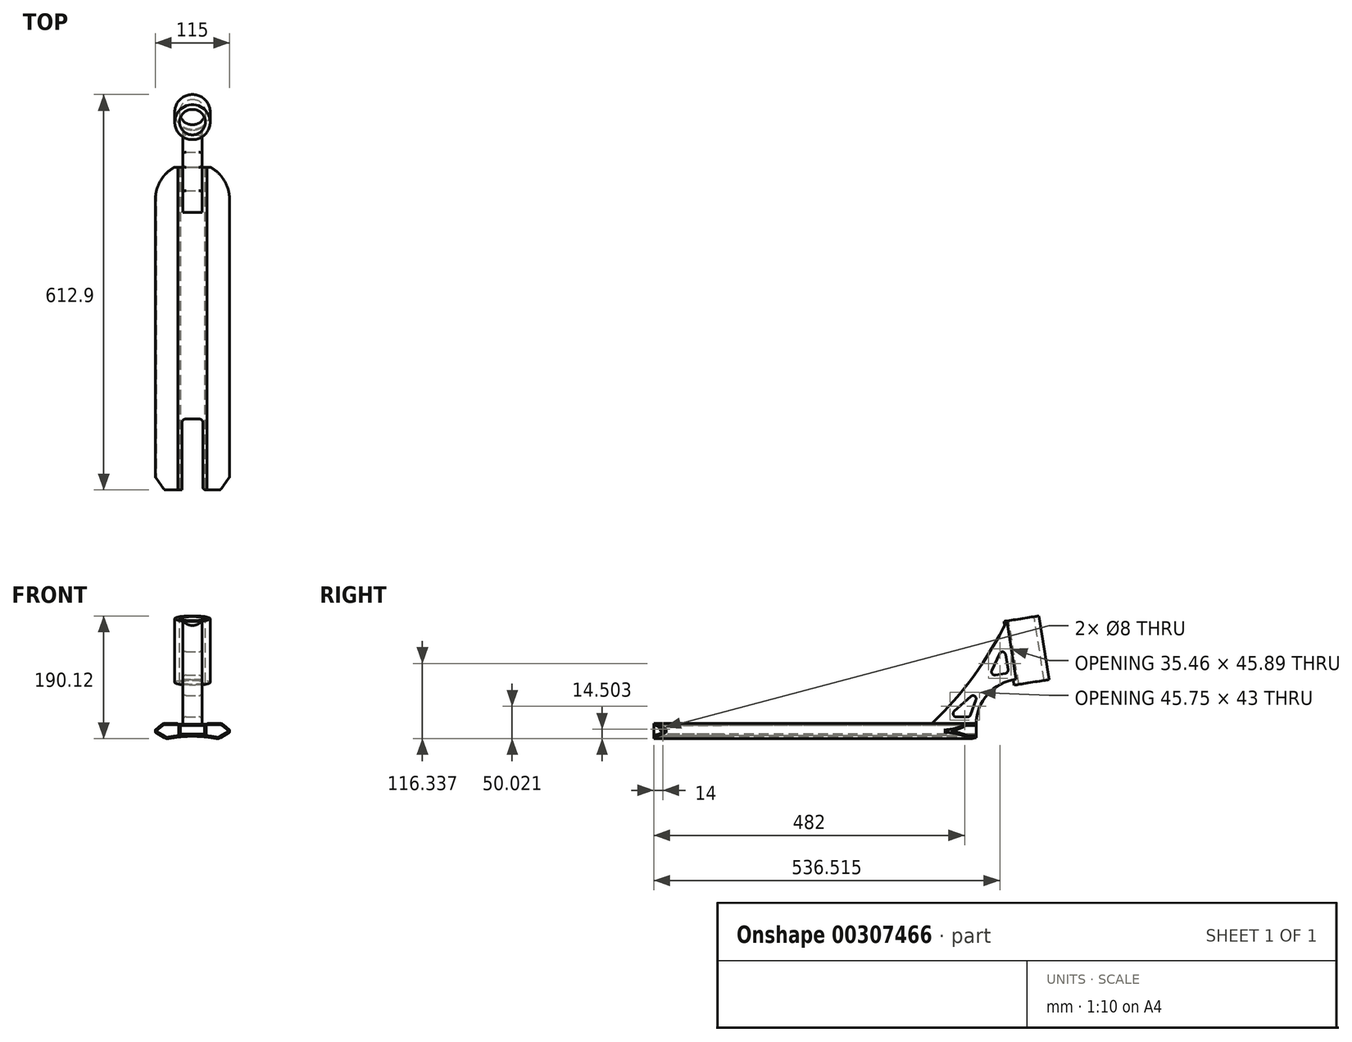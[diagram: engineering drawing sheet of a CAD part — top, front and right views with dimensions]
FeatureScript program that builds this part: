
annotation { "Feature Type Name" : "Feature", "Feature Type Description" : "" }
export const myFeature = defineFeature(function(context is Context, id is Id, definition is map)
    precondition{}
    {
        {
            var Q0;
            Q0=qCreatedBy(makeId("Front.planeOp"),FACE);
            var sketch = newSketch(context, id + "F0", { "sketchPlane" : qUnion([Q0])});
            skLineSegment(sketch, "E0", {"start": v(0, 0) * mm, "end": v(0, 75.33) * mm, "construction": true});
            skLineSegment(sketch, "E1", {"start": v(0, 22.7) * mm, "end": v(22.5, 22.7) * mm});
            skLineSegment(sketch, "E2", {"start": v(22.5, 24) * mm, "end": v(22.5, 22.7) * mm});
            skLineSegment(sketch, "E3", {"start": v(45.58, 24) * mm, "end": v(22.5, 24) * mm});
            skLineSegment(sketch, "E4", {"start": v(57.5, 14) * mm, "end": v(45.58, 24) * mm});
            skLineSegment(sketch, "E5", {"start": v(57.5, 14) * mm, "end": v(57.5, 10) * mm});
            skLineSegment(sketch, "E6", {"start": v(57.5, 10) * mm, "end": v(40.18, 0) * mm});
            skLineSegment(sketch, "E7.MirrorCS", {"start": v(0, 22.7) * mm, "end": v(-22.5, 22.7) * mm});
            skLineSegment(sketch, "E8.MirrorCS", {"start": v(-45.58, 24) * mm, "end": v(-22.5, 24) * mm});
            skLineSegment(sketch, "E9.MirrorCS", {"start": v(-22.5, 24) * mm, "end": v(-22.5, 22.7) * mm});
            skLineSegment(sketch, "E10.MirrorCS", {"start": v(-57.5, 14) * mm, "end": v(-45.58, 24) * mm});
            skLineSegment(sketch, "E11.MirrorCS", {"start": v(-57.5, 14) * mm, "end": v(-57.5, 10) * mm});
            skLineSegment(sketch, "E12.MirrorCS", {"start": v(-57.5, 10) * mm, "end": v(-40.18, 0) * mm});
            skArc(sketch, "E13", {"start": v(40.18, 0) * mm, "mid": v(0, 4.08) * mm, "end": v(-40.18, 0) * mm});
            skSolve(sketch);
        }
        {
            var Q0;
            Q0 = qSketchRegion(id + "F0", true);
            extrude(context, id + "F1", {"entities" : qUnion([Q0]), "endBound" : BoundingType.SYMMETRIC, "depth" : 500 * mm});
        }
        {
            var Q0;
            Q0=qCreatedBy(makeId("Front.planeOp"),FACE);
            var sketch = newSketch(context, id + "F2", { "sketchPlane" : qUnion([Q0])});
            skLineSegment(sketch, "E14.bottom", {"start": v(-19, 20.7) * mm, "end": v(19, 20.7) * mm});
            skLineSegment(sketch, "E14.top", {"start": v(-19, 7.7) * mm, "end": v(19, 7.7) * mm});
            skLineSegment(sketch, "E14.left", {"start": v(-19, 20.7) * mm, "end": v(-19, 7.7) * mm});
            skLineSegment(sketch, "E14.right", {"start": v(19, 20.7) * mm, "end": v(19, 7.7) * mm});
            skSolve(sketch);
        }
        {
            var Q0;
            Q0 = qSketchRegion(id + "F2", true);
            extrude(context, id + "F3", {"entities" : qUnion([Q0]), "operationType" : NewBodyOperationType.REMOVE, "endBound" : BoundingType.SYMMETRIC, "oppositeDirection" : true, "depth" : 500 * mm});
        }
        {
            var Q0;
            Q0=makeQuery(id+"F1.opExtrude","SWEPT_EDGE",EDGE,{"disambiguationData":[OSD([sQuery(id+"F0.wireOp",EDGE,"E6"),sQuery(id+"F0.wireOp",EDGE,"E13")])]});
            var Q1;
            Q1=makeQuery(id+"F1.opExtrude","SWEPT_EDGE",EDGE,{"disambiguationData":[OSD([sQuery(id+"F0.wireOp",EDGE,"E12.MirrorCS"),sQuery(id+"F0.wireOp",EDGE,"E13")])]});
            var Q2;
            Q2=makeQuery(id+"F1.opExtrude","SWEPT_EDGE",EDGE,{"disambiguationData":[OSD([sQuery(id+"F0.wireOp",EDGE,"E8.MirrorCS"),sQuery(id+"F0.wireOp",EDGE,"E10.MirrorCS")])]});
            var Q3;
            Q3=makeQuery(id+"F1.opExtrude","SWEPT_EDGE",EDGE,{"disambiguationData":[OSD([sQuery(id+"F0.wireOp",EDGE,"E3"),sQuery(id+"F0.wireOp",EDGE,"E4")])]});
            fillet(context, id + "F4", {"entities" : qUnion([Q0, Q1, Q2, Q3]), "radius" : 9 * mm, "tangentPropagation" : true, "allowEdgeOverflow" : false});
        }
        {
            var Q0;
            Q0=makeQuery(id+"F1.opExtrude","SWEPT_EDGE",EDGE,{"disambiguationData":[OSD([sQuery(id+"F0.wireOp",EDGE,"E4"),sQuery(id+"F0.wireOp",EDGE,"E5")])]});
            var Q1;
            Q1=makeQuery(id+"F1.opExtrude","SWEPT_EDGE",EDGE,{"disambiguationData":[OSD([sQuery(id+"F0.wireOp",EDGE,"E5"),sQuery(id+"F0.wireOp",EDGE,"E6")])]});
            var Q2;
            Q2=makeQuery(id+"F1.opExtrude","SWEPT_EDGE",EDGE,{"disambiguationData":[OSD([sQuery(id+"F0.wireOp",EDGE,"E10.MirrorCS"),sQuery(id+"F0.wireOp",EDGE,"E11.MirrorCS")])]});
            var Q3;
            Q3=makeQuery(id+"F1.opExtrude","SWEPT_EDGE",EDGE,{"disambiguationData":[OSD([sQuery(id+"F0.wireOp",EDGE,"E11.MirrorCS"),sQuery(id+"F0.wireOp",EDGE,"E12.MirrorCS")])]});
            fillet(context, id + "F5", {"entities" : qUnion([Q0, Q1, Q2, Q3]), "radius" : 1 * mm, "tangentPropagation" : true, "allowEdgeOverflow" : false});
        }
        {
            var Q0;
            Q0=makeQuery(id+"F1.opExtrude","SWEPT_EDGE",EDGE,{"disambiguationData":[OSD([sQuery(id+"F0.wireOp",EDGE,"E8.MirrorCS"),sQuery(id+"F0.wireOp",EDGE,"E9.MirrorCS")])]});
            var Q1;
            Q1=makeQuery(id+"F1.opExtrude","SWEPT_EDGE",EDGE,{"disambiguationData":[OSD([sQuery(id+"F0.wireOp",EDGE,"E2"),sQuery(id+"F0.wireOp",EDGE,"E3")])]});
            fillet(context, id + "F6", {"entities" : qUnion([Q0, Q1]), "radius" : 2 * mm, "tangentPropagation" : true, "allowEdgeOverflow" : false});
        }
        {
            var Q0;
            Q0=makeQuery(id+"F1.opExtrude","CAP_FACE",FACE,{"disambiguationData":[OSD([sQuery(id+"F0.wireOp",EDGE,"E1"),sQuery(id+"F0.wireOp",EDGE,"E2"),sQuery(id+"F0.wireOp",EDGE,"E3"),sQuery(id+"F0.wireOp",EDGE,"E4"),sQuery(id+"F0.wireOp",EDGE,"E5"),sQuery(id+"F0.wireOp",EDGE,"E6"),sQuery(id+"F0.wireOp",EDGE,"E7.MirrorCS"),sQuery(id+"F0.wireOp",EDGE,"E8.MirrorCS"),sQuery(id+"F0.wireOp",EDGE,"E9.MirrorCS"),sQuery(id+"F0.wireOp",EDGE,"E10.MirrorCS"),sQuery(id+"F0.wireOp",EDGE,"E11.MirrorCS"),sQuery(id+"F0.wireOp",EDGE,"E12.MirrorCS"),sQuery(id+"F0.wireOp",EDGE,"E13")])],"isStart":false});
            var sketch = newSketch(context, id + "F7", { "sketchPlane" : qUnion([Q0])});
            skLineSegment(sketch, "E15.0", {"start": v(-42.3, 22) * mm, "end": v(-24.37, 22) * mm});
            skArc(sketch, "E15.1", {"start": v(-42.3, 22) * mm, "mid": v(-44.7, 21.58) * mm, "end": v(-46.8, 20.36) * mm});
            skArc(sketch, "E15.2", {"start": v(37.3, 2.6) * mm, "mid": v(0, 6.08) * mm, "end": v(-37.3, 2.6) * mm});
            skArc(sketch, "E15.3", {"start": v(-42.1, 3.42) * mm, "mid": v(-39.78, 2.58) * mm, "end": v(-37.3, 2.6) * mm});
            skLineSegment(sketch, "E15.4", {"start": v(-55.61, 11.22) * mm, "end": v(-42.1, 3.42) * mm});
            skLineSegment(sketch, "E15.5", {"start": v(-55.76, 12.85) * mm, "end": v(-46.8, 20.36) * mm});
            skPoint(sketch, "E16.visualSharp", {"position": v(-56.85, 11.93) * mm});
            skArc(sketch, "E16.filletArc", {"start": v(-55.76, 12.85) * mm, "mid": v(-56.1, 12) * mm, "end": v(-55.61, 11.22) * mm});
            skArc(sketch, "E17", {"start": v(-22.5, 20.7) * mm, "mid": v(-23.23, 21.64) * mm, "end": v(-24.37, 22) * mm});
            skLineSegment(sketch, "E18", {"start": v(-22.5, 20.7) * mm, "end": v(-21, 20.7) * mm});
            skLineSegment(sketch, "E19", {"start": v(-21, 20.7) * mm, "end": v(-21, 4.98) * mm});
            skLineSegment(sketch, "E20.MirrorCS", {"start": v(21, 20.7) * mm, "end": v(21, 4.98) * mm});
            skLineSegment(sketch, "E21.MirrorCS", {"start": v(22.5, 20.7) * mm, "end": v(21, 20.7) * mm});
            skArc(sketch, "E22.MirrorCS", {"start": v(22.5, 20.7) * mm, "mid": v(23.23, 21.64) * mm, "end": v(24.37, 22) * mm});
            skLineSegment(sketch, "E23.MirrorCS", {"start": v(42.3, 22) * mm, "end": v(24.37, 22) * mm});
            skArc(sketch, "E24.MirrorCS", {"start": v(42.3, 22) * mm, "mid": v(44.7, 21.58) * mm, "end": v(46.8, 20.36) * mm});
            skLineSegment(sketch, "E25.MirrorCS", {"start": v(55.76, 12.85) * mm, "end": v(46.8, 20.36) * mm});
            skArc(sketch, "E26.MirrorCS", {"start": v(55.76, 12.85) * mm, "mid": v(56.1, 12) * mm, "end": v(55.61, 11.22) * mm});
            skLineSegment(sketch, "E27.MirrorCS", {"start": v(55.61, 11.22) * mm, "end": v(42.1, 3.42) * mm});
            skArc(sketch, "E28.MirrorCS", {"start": v(42.1, 3.42) * mm, "mid": v(39.78, 2.58) * mm, "end": v(37.3, 2.6) * mm});
            skArc(sketch, "E29.MirrorCS", {"start": v(-37.3, 2.6) * mm, "mid": v(0, 6.08) * mm, "end": v(37.3, 2.6) * mm});
            skSolve(sketch);
        }
        {
            var Q0;
            Q0=makeQuery(id+"F7.imprint","IMPRINT",FACE,{"disambiguationData":[TD([[makeQuery(id+"F7.imprint","IMPRINT",EDGE,{"derivedFrom":sQuery(id+"F7.wireOp",EDGE,"E15.0")}),-1.0]])]});
            var Q1;
            {var subQ0=sQuery(id+"F7.wireOp",EDGE,"E20.MirrorCS");Q1=makeQuery(id+"F7.imprint","IMPRINT",FACE,{"disambiguationData":[TD([[makeQuery(id+"F7.imprint","IMPRINT",EDGE,{"derivedFrom":subQ0}),1.0]])]});}
            extrude(context, id + "F8", {"entities" : qUnion([Q0, Q1]), "operationType" : NewBodyOperationType.REMOVE, "endBound" : BoundingType.THROUGH_ALL, "oppositeDirection" : true, "depth" : 25 * mm});
        }
        {
            var Q0;
            Q0=qCreatedBy(makeId("Top.planeOp"),FACE);
            var sketch = newSketch(context, id + "F9", { "sketchPlane" : qUnion([Q0])});
            skArc(sketch, "E30", {"start": v(57.5, 200) * mm, "mid": v(0, 257.5) * mm, "end": v(-57.5, 200) * mm});
            skLineSegment(sketch, "E31", {"start": v(-57.5, 200) * mm, "end": v(-57.5, 280) * mm});
            skLineSegment(sketch, "E32", {"start": v(57.5, 200) * mm, "end": v(57.5, 280) * mm});
            skLineSegment(sketch, "E33", {"start": v(-57.5, 280) * mm, "end": v(57.5, 280) * mm});
            skSolve(sketch);
        }
        {
            var Q0;
            Q0 = qSketchRegion(id + "F9", true);
            extrude(context, id + "F10", {"entities" : qUnion([Q0]), "operationType" : NewBodyOperationType.REMOVE, "endBound" : BoundingType.THROUGH_ALL, "oppositeDirection" : true, "depth" : 25 * mm, "hasSecondDirection" : true, "secondDirectionBound" : SecondDirectionBoundingType.THROUGH_ALL, "secondDirectionOppositeDirection" : false, "secondDirectionDepth" : 25 * mm});
        }
        {
            var Q0;
            Q0=qCreatedBy(makeId("Top.planeOp"),FACE);
            var sketch = newSketch(context, id + "F11", { "sketchPlane" : qUnion([Q0])});
            skLineSegment(sketch, "E34", {"start": v(-68, -216) * mm, "end": v(-68, -346) * mm});
            skLineSegment(sketch, "E35", {"start": v(-68, -346) * mm, "end": v(68, -346) * mm});
            skLineSegment(sketch, "E36", {"start": v(68, -346) * mm, "end": v(68, -216) * mm});
            skLineSegment(sketch, "E37", {"start": v(68, -216) * mm, "end": v(43.3, -250) * mm});
            skLineSegment(sketch, "E38", {"start": v(43.3, -250) * mm, "end": v(16, -250) * mm});
            skLineSegment(sketch, "E39", {"start": v(16, -250) * mm, "end": v(16, -140) * mm});
            skLineSegment(sketch, "E40", {"start": v(16, -140) * mm, "end": v(-16, -140) * mm});
            skLineSegment(sketch, "E41", {"start": v(-16, -140) * mm, "end": v(-16, -250) * mm});
            skLineSegment(sketch, "E42", {"start": v(-16, -250) * mm, "end": v(-43.3, -250) * mm});
            skLineSegment(sketch, "E43", {"start": v(-43.3, -250) * mm, "end": v(-68, -216) * mm});
            skSolve(sketch);
        }
        {
            var Q0;
            Q0 = qSketchRegion(id + "F11", true);
            extrude(context, id + "F12", {"entities" : qUnion([Q0]), "operationType" : NewBodyOperationType.REMOVE, "endBound" : BoundingType.THROUGH_ALL, "oppositeDirection" : true, "depth" : 25 * mm, "hasSecondDirection" : true, "secondDirectionBound" : SecondDirectionBoundingType.THROUGH_ALL, "secondDirectionOppositeDirection" : false, "secondDirectionDepth" : 25 * mm});
        }
        {
            var Q0;
            {var subQ0=sQuery(id+"F11.wireOp",EDGE,"E40");var subQ1=sQuery(id+"F11.wireOp",EDGE,"E41");Q0=makeQuery(id+"F12.boolean.opBoolean","COPY",EDGE,{"disambiguationData":[TD([makeQuery(id+"F3.boolean.opBoolean","COPY",FACE,{"derivedFrom":makeQuery(id+"F3.opExtrude","SWEPT_FACE",FACE,{"disambiguationData":[OSD([sQuery(id+"F2.wireOp",EDGE,"E14.bottom")])]})})])],"derivedFrom":makeQuery(id+"F12.opExtrude","SWEPT_EDGE",EDGE,{"disambiguationData":[OSD([subQ0,subQ1])]})});}
            var Q1;
            {var subQ0=sQuery(id+"F11.wireOp",EDGE,"E41");var subQ1=sQuery(id+"F11.wireOp",EDGE,"E40");Q1=makeQuery(id+"F12.boolean.opBoolean","COPY",EDGE,{"disambiguationData":[TD([makeQuery(id+"F1.opExtrude","SWEPT_FACE",FACE,{"disambiguationData":[OSD([sQuery(id+"F0.wireOp",EDGE,"E13")])]})])],"derivedFrom":makeQuery(id+"F12.opExtrude","SWEPT_EDGE",EDGE,{"disambiguationData":[OSD([subQ1,subQ0])]})});}
            var Q2;
            {var subQ0=sQuery(id+"F11.wireOp",EDGE,"E40");var subQ1=sQuery(id+"F11.wireOp",EDGE,"E39");Q2=makeQuery(id+"F12.boolean.opBoolean","COPY",EDGE,{"disambiguationData":[TD([makeQuery(id+"F3.boolean.opBoolean","COPY",FACE,{"derivedFrom":makeQuery(id+"F3.opExtrude","SWEPT_FACE",FACE,{"disambiguationData":[OSD([sQuery(id+"F2.wireOp",EDGE,"E14.bottom")])]})})])],"derivedFrom":makeQuery(id+"F12.opExtrude","SWEPT_EDGE",EDGE,{"disambiguationData":[OSD([subQ1,subQ0])]})});}
            var Q3;
            {var subQ0=sQuery(id+"F11.wireOp",EDGE,"E39");var subQ1=sQuery(id+"F11.wireOp",EDGE,"E40");Q3=makeQuery(id+"F12.boolean.opBoolean","COPY",EDGE,{"disambiguationData":[TD([makeQuery(id+"F1.opExtrude","SWEPT_FACE",FACE,{"disambiguationData":[OSD([sQuery(id+"F0.wireOp",EDGE,"E13")])]})])],"derivedFrom":makeQuery(id+"F12.opExtrude","SWEPT_EDGE",EDGE,{"disambiguationData":[OSD([subQ0,subQ1])]})});}
            var Q4;
            {var subQ2=sQuery(id+"F11.wireOp",EDGE,"E41");Q4=makeQuery(id+"F12.boolean.opBoolean","COPY",EDGE,{"disambiguationData":[TD([makeQuery(id+"F3.boolean.opBoolean","COPY",FACE,{"derivedFrom":makeQuery(id+"F3.opExtrude","SWEPT_FACE",FACE,{"disambiguationData":[OSD([sQuery(id+"F2.wireOp",EDGE,"E14.bottom")])]})})])],"derivedFrom":makeQuery(id+"F12.opExtrude","SWEPT_EDGE",EDGE,{"disambiguationData":[OSD([subQ2,sQuery(id+"F11.wireOp",EDGE,"E42")])]})});}
            var Q5;
            {var subQ0=sQuery(id+"F0.wireOp",EDGE,"E13");var subQ1=sQuery(id+"F11.wireOp",EDGE,"E41");Q5=makeQuery(id+"F12.boolean.opBoolean","COPY",EDGE,{"disambiguationData":[TD([makeQuery(id+"F1.opExtrude","SWEPT_FACE",FACE,{"disambiguationData":[OSD([subQ0])]})])],"derivedFrom":makeQuery(id+"F12.opExtrude","SWEPT_EDGE",EDGE,{"disambiguationData":[OSD([subQ1,sQuery(id+"F11.wireOp",EDGE,"E42")])]})});}
            var Q6;
            {var subQ0=sQuery(id+"F0.wireOp",EDGE,"E13");var subQ1=sQuery(id+"F11.wireOp",EDGE,"E39");Q6=makeQuery(id+"F12.boolean.opBoolean","COPY",EDGE,{"disambiguationData":[TD([makeQuery(id+"F1.opExtrude","SWEPT_FACE",FACE,{"disambiguationData":[OSD([subQ0])]})])],"derivedFrom":makeQuery(id+"F12.opExtrude","SWEPT_EDGE",EDGE,{"disambiguationData":[OSD([sQuery(id+"F11.wireOp",EDGE,"E38"),subQ1])]})});}
            var Q7;
            {var subQ2=sQuery(id+"F11.wireOp",EDGE,"E39");Q7=makeQuery(id+"F12.boolean.opBoolean","COPY",EDGE,{"disambiguationData":[TD([makeQuery(id+"F3.boolean.opBoolean","COPY",FACE,{"derivedFrom":makeQuery(id+"F3.opExtrude","SWEPT_FACE",FACE,{"disambiguationData":[OSD([sQuery(id+"F2.wireOp",EDGE,"E14.bottom")])]})})])],"derivedFrom":makeQuery(id+"F12.opExtrude","SWEPT_EDGE",EDGE,{"disambiguationData":[OSD([sQuery(id+"F11.wireOp",EDGE,"E38"),subQ2])]})});}
            fillet(context, id + "F13", {"entities" : qUnion([Q0, Q1, Q2, Q3, Q4, Q5, Q6, Q7]), "radius" : 5 * mm, "tangentPropagation" : true, "allowEdgeOverflow" : false});
        }
        {
            var Q0;
            Q0=qCreatedBy(makeId("Right.planeOp"),FACE);
            var sketch = newSketch(context, id + "F14", { "sketchPlane" : qUnion([Q0])});
            skLineSegment(sketch, "E44", {"start": v(180, 22.7) * mm, "end": v(250, 22.7) * mm});
            skArc(sketch, "E45", {"start": v(311.71, 92.2) * mm, "mid": v(267.66, 69.18) * mm, "end": v(250, 22.7) * mm});
            skArc(sketch, "E46", {"start": v(180, 22.7) * mm, "mid": v(245.97, 97.36) * mm, "end": v(297.38, 182.7) * mm});
            skLineSegment(sketch, "E47", {"start": v(297.38, 182.7) * mm, "end": v(342.82, 189.9) * mm});
            skLineSegment(sketch, "E48", {"start": v(342.82, 189.9) * mm, "end": v(358.46, 91.13) * mm});
            skLineSegment(sketch, "E49", {"start": v(358.46, 91.13) * mm, "end": v(313.03, 83.93) * mm});
            skLineSegment(sketch, "E50", {"start": v(313.03, 83.93) * mm, "end": v(311.71, 92.2) * mm});
            skSolve(sketch);
        }
        {
            var Q0;
            Q0=makeQuery(id+"F14.imprint","IMPRINT",FACE,{"disambiguationData":[TD([[makeQuery(id+"F14.imprint","IMPRINT",EDGE,{"derivedFrom":sQuery(id+"F14.wireOp",EDGE,"E44")}),1.0]])]});
            extrude(context, id + "F15", {"entities" : qUnion([Q0]), "operationType" : NewBodyOperationType.ADD, "endBound" : BoundingType.SYMMETRIC, "depth" : 30 * mm});
        }
        {
            var Q0;
            Q0=makeQuery(id+"F15.opExtrude","SWEPT_FACE",FACE,{"disambiguationData":[OSD([sQuery(id+"F14.wireOp",EDGE,"E47")])]});
            var sketch = newSketch(context, id + "F16", { "sketchPlane" : qUnion([Q0])});
            skCircle(sketch, "E51", {"center": v(0, 345.3) * mm, "radius": 27.5 * mm});
            skSolve(sketch);
        }
        {
            var Q0;
            Q0 = qSketchRegion(id + "F16", true);
            var Q1;
            Q1=makeQuery(id+"F15.opExtrude","SWEPT_FACE",FACE,{"disambiguationData":[OSD([sQuery(id+"F14.wireOp",EDGE,"E49")])]});
            extrude(context, id + "F17", {"entities" : qUnion([Q0]), "operationType" : NewBodyOperationType.ADD, "endBound" : BoundingType.UP_TO_SURFACE, "oppositeDirection" : true, "endBoundEntityFace" : qUnion([Q1]), "depth" : 25 * mm});
        }
        {
            var Q0;
            Q0=makeQuery(id+"F17.boolean.opBoolean","MERGE",FACE,{"derivedFrom":[makeQuery(id+"F15.opExtrude","SWEPT_FACE",FACE,{"disambiguationData":[OSD([sQuery(id+"F14.wireOp",EDGE,"E47")])]}),makeQuery(id+"F17.opExtrude","CAP_FACE",FACE,{"disambiguationData":[OSD([sQuery(id+"F16.wireOp",EDGE,"E51")])],"isStart":true})]});
            var sketch = newSketch(context, id + "F18", { "sketchPlane" : qUnion([Q0])});
            skPoint(sketch, "E52", {"position": v(0, 345.3) * mm});
            skSolve(sketch);
        }
        {
            var Q0;
            Q0=sQuery(id+"F18.wireOp",VERTEX,"E52");
            var Q1;
            Q1=makeQuery(id+"F1.opExtrude","SWEPT_BODY",BODY,{"disambiguationData":[OSD([sQuery(id+"F0.wireOp",EDGE,"E1"),sQuery(id+"F0.wireOp",EDGE,"E2"),sQuery(id+"F0.wireOp",EDGE,"E3"),sQuery(id+"F0.wireOp",EDGE,"E4"),sQuery(id+"F0.wireOp",EDGE,"E5"),sQuery(id+"F0.wireOp",EDGE,"E6"),sQuery(id+"F0.wireOp",EDGE,"E7.MirrorCS"),sQuery(id+"F0.wireOp",EDGE,"E8.MirrorCS"),sQuery(id+"F0.wireOp",EDGE,"E9.MirrorCS"),sQuery(id+"F0.wireOp",EDGE,"E10.MirrorCS"),sQuery(id+"F0.wireOp",EDGE,"E11.MirrorCS"),sQuery(id+"F0.wireOp",EDGE,"E12.MirrorCS"),sQuery(id+"F0.wireOp",EDGE,"E13")])]});
            hole(context, id + "F19", {"style" : HoleStyle.SIMPLE, "endStyle" : HoleEndStyle.THROUGH, "holeDiameter" : 40 * mm, "isTappedThrough" : true, "tappedDepth" : 12 * mm, "tapClearance" : 3, "locations" : qUnion([Q0]), "scope" : qUnion([Q1])});
        }
        {
            var Q0;
            Q0=makeQuery(id+"F8.boolean.opBoolean","COPY",FACE,{"derivedFrom":makeQuery(id+"F8.opExtrude","SWEPT_FACE",FACE,{"disambiguationData":[OSD([sQuery(id+"F7.wireOp",EDGE,"E20.MirrorCS")])]})});
            var sketch = newSketch(context, id + "F20", { "sketchPlane" : qUnion([Q0])});
            skPoint(sketch, "E53", {"position": v(-236, 14.98) * mm});
            skPoint(sketch, "E54", {"position": v(-250, 14.98) * mm});
            skSolve(sketch);
        }
        {
            var Q0;
            Q0=sQuery(id+"F20.wireOp",VERTEX,"E53");
            var Q1;
            Q1=makeQuery(id+"F1.opExtrude","SWEPT_BODY",BODY,{"disambiguationData":[OSD([sQuery(id+"F0.wireOp",EDGE,"E1"),sQuery(id+"F0.wireOp",EDGE,"E2"),sQuery(id+"F0.wireOp",EDGE,"E3"),sQuery(id+"F0.wireOp",EDGE,"E4"),sQuery(id+"F0.wireOp",EDGE,"E5"),sQuery(id+"F0.wireOp",EDGE,"E6"),sQuery(id+"F0.wireOp",EDGE,"E7.MirrorCS"),sQuery(id+"F0.wireOp",EDGE,"E8.MirrorCS"),sQuery(id+"F0.wireOp",EDGE,"E9.MirrorCS"),sQuery(id+"F0.wireOp",EDGE,"E10.MirrorCS"),sQuery(id+"F0.wireOp",EDGE,"E11.MirrorCS"),sQuery(id+"F0.wireOp",EDGE,"E12.MirrorCS"),sQuery(id+"F0.wireOp",EDGE,"E13")])]});
            hole(context, id + "F21", {"style" : HoleStyle.SIMPLE, "endStyle" : HoleEndStyle.BLIND, "holeDiameter" : 8 * mm, "holeDepth" : 50 * mm, "isTappedThrough" : true, "tappedDepth" : 12 * mm, "tapClearance" : 3, "locations" : qUnion([Q0]), "scope" : qUnion([Q1])});
        }
        {
            var Q0;
            Q0=makeQuery(id+"F15.opExtrude","CAP_FACE",FACE,{"disambiguationData":[OSD([sQuery(id+"F14.wireOp",EDGE,"E44"),sQuery(id+"F14.wireOp",EDGE,"E45"),sQuery(id+"F14.wireOp",EDGE,"E46"),sQuery(id+"F14.wireOp",EDGE,"E47"),sQuery(id+"F14.wireOp",EDGE,"E48"),sQuery(id+"F14.wireOp",EDGE,"E49"),sQuery(id+"F14.wireOp",EDGE,"E50")])],"isStart":false});
            var sketch = newSketch(context, id + "F22", { "sketchPlane" : qUnion([Q0])});
            skLineSegment(sketch, "E55", {"start": v(270.34, 97.42) * mm, "end": v(299.97, 102.11) * mm});
            skLineSegment(sketch, "E56", {"start": v(299.97, 102.11) * mm, "end": v(292.84, 147.11) * mm});
            skLineSegment(sketch, "E57", {"start": v(270.34, 97.42) * mm, "end": v(292.84, 147.11) * mm});
            skLineSegment(sketch, "E58", {"start": v(206, 34) * mm, "end": v(240, 34) * mm});
            skLineSegment(sketch, "E59", {"start": v(240, 34) * mm, "end": v(256.38, 79) * mm});
            skLineSegment(sketch, "E60", {"start": v(206, 34) * mm, "end": v(256.38, 79) * mm});
            skSolve(sketch);
        }
        {
            var Q0;
            Q0 = qSketchRegion(id + "F22", true);
            extrude(context, id + "F23", {"entities" : qUnion([Q0]), "operationType" : NewBodyOperationType.REMOVE, "endBound" : BoundingType.THROUGH_ALL, "oppositeDirection" : true, "depth" : 25 * mm});
        }
        {
            var Q0;
            Q0=makeQuery(id+"F23.boolean.opBoolean","COPY",FACE,{"derivedFrom":makeQuery(id+"F23.opExtrude","SWEPT_FACE",FACE,{"disambiguationData":[OSD([sQuery(id+"F22.wireOp",EDGE,"E59")])]})});
            var Q1;
            Q1=makeQuery(id+"F23.boolean.opBoolean","COPY",FACE,{"derivedFrom":makeQuery(id+"F23.opExtrude","SWEPT_FACE",FACE,{"disambiguationData":[OSD([sQuery(id+"F22.wireOp",EDGE,"E56")])]})});
            var Q2;
            Q2=makeQuery(id+"F23.boolean.opBoolean","COPY",FACE,{"derivedFrom":makeQuery(id+"F23.opExtrude","SWEPT_FACE",FACE,{"disambiguationData":[OSD([sQuery(id+"F22.wireOp",EDGE,"E57")])]})});
            var Q3;
            Q3=makeQuery(id+"F23.boolean.opBoolean","COPY",FACE,{"derivedFrom":makeQuery(id+"F23.opExtrude","SWEPT_FACE",FACE,{"disambiguationData":[OSD([sQuery(id+"F22.wireOp",EDGE,"E60")])]})});
            var Q4;
            Q4=makeQuery(id+"F23.boolean.opBoolean","COPY",FACE,{"derivedFrom":makeQuery(id+"F23.opExtrude","SWEPT_FACE",FACE,{"disambiguationData":[OSD([sQuery(id+"F22.wireOp",EDGE,"E58")])]})});
            var Q5;
            Q5=makeQuery(id+"F23.boolean.opBoolean","COPY",FACE,{"derivedFrom":makeQuery(id+"F23.opExtrude","SWEPT_FACE",FACE,{"disambiguationData":[OSD([sQuery(id+"F22.wireOp",EDGE,"E55")])]})});
            fillet(context, id + "F24", {"entities" : qUnion([Q0, Q1, Q2, Q3, Q4, Q5]), "radius" : 5 * mm, "tangentPropagation" : true, "allowEdgeOverflow" : false});
        }
    });
